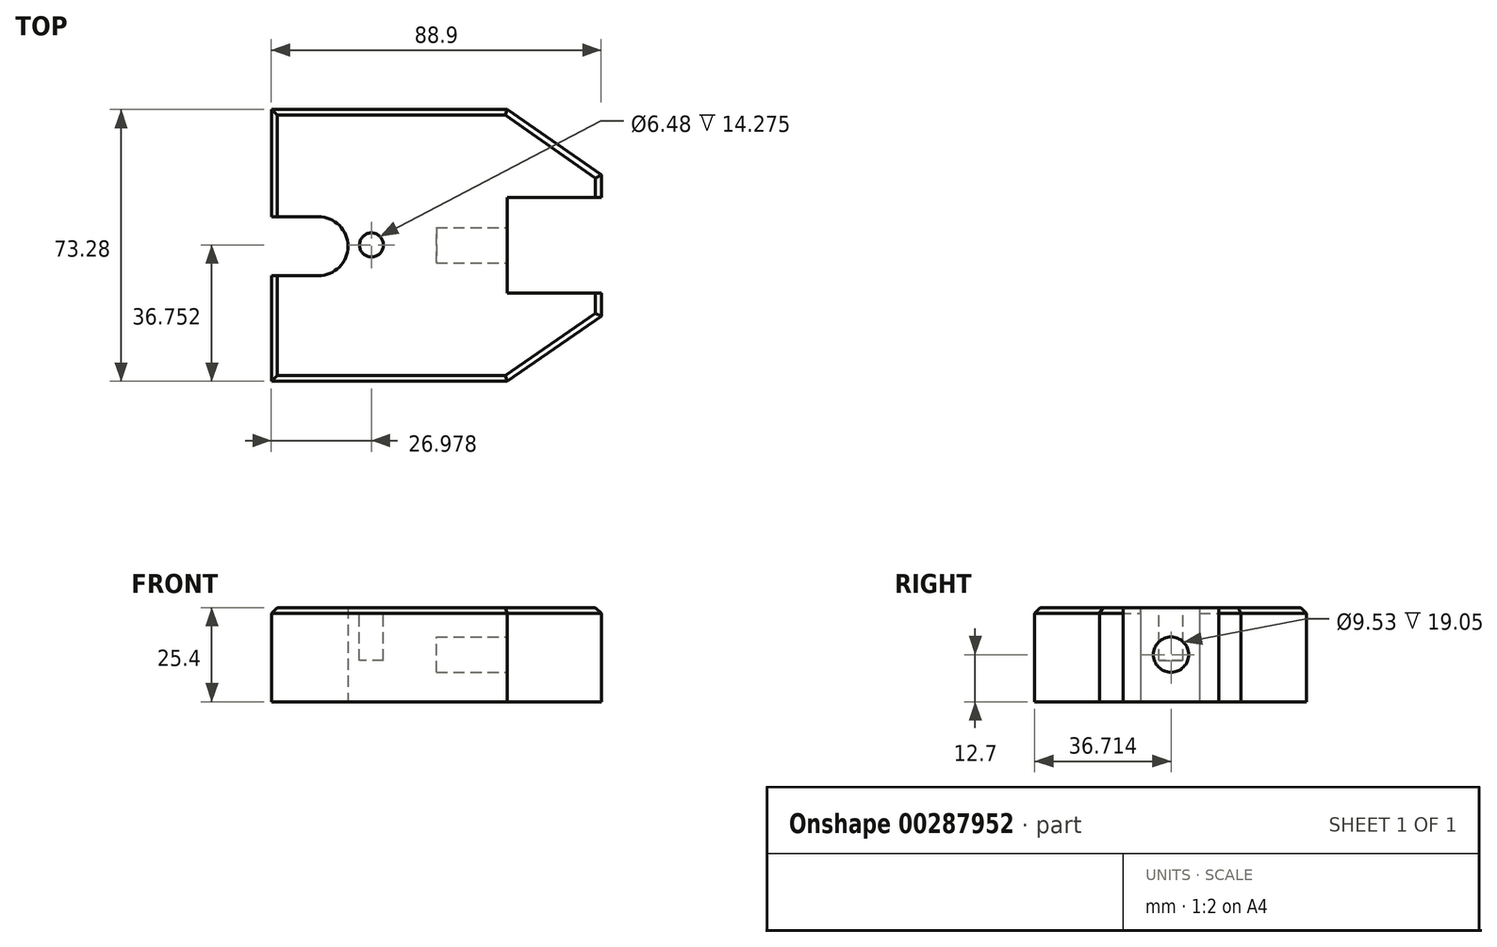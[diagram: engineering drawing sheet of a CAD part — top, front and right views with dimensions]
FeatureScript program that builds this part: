
annotation { "Feature Type Name" : "Feature", "Feature Type Description" : "" }
export const myFeature = defineFeature(function(context is Context, id is Id, definition is map)
    precondition{}
    {
        {
            var Q0;
            Q0=qCreatedBy(makeId("Top.planeOp"),FACE);
            var sketch = newSketch(context, id + "F0", { "sketchPlane" : qUnion([Q0])});
            skLineSegment(sketch, "E0.bottom", {"start": v(-102.85, 91.05) * mm, "end": v(-13.95, 91.05) * mm});
            skLineSegment(sketch, "E0.top", {"start": v(-102.85, 17.77) * mm, "end": v(-13.95, 17.77) * mm});
            skLineSegment(sketch, "E0.left", {"start": v(-102.85, 91.05) * mm, "end": v(-102.85, 17.77) * mm});
            skLineSegment(sketch, "E0.right", {"start": v(-13.95, 91.05) * mm, "end": v(-13.95, 17.77) * mm});
            skLineSegment(sketch, "E1.bottom", {"start": v(-13.95, 67.37) * mm, "end": v(-39.35, 67.37) * mm});
            skLineSegment(sketch, "E1.top", {"start": v(-13.95, 41.6) * mm, "end": v(-39.35, 41.6) * mm});
            skLineSegment(sketch, "E1.left", {"start": v(-13.95, 67.37) * mm, "end": v(-13.95, 41.6) * mm});
            skLineSegment(sketch, "E1.right", {"start": v(-39.35, 67.37) * mm, "end": v(-39.35, 41.6) * mm});
            skLineSegment(sketch, "E2", {"start": v(-13.95, 73.4) * mm, "end": v(-39.35, 91.05) * mm});
            skLineSegment(sketch, "E3", {"start": v(-13.95, 35.3) * mm, "end": v(-39.35, 17.77) * mm});
            skLineSegment(sketch, "E4", {"start": v(-133.5, 54.52) * mm, "end": v(33.35, 54.52) * mm, "construction": true});
            skLineSegment(sketch, "E5", {"start": v(-90.15, 65.78) * mm, "end": v(-90.15, 42.58) * mm, "construction": true});
            skArc(sketch, "E6", {"start": v(-90.15, 46.23) * mm, "mid": v(-82.2, 54.18) * mm, "end": v(-90.15, 62.13) * mm});
            skLineSegment(sketch, "E7", {"start": v(-90.15, 62.13) * mm, "end": v(-102.85, 62.13) * mm});
            skLineSegment(sketch, "E8", {"start": v(-102.85, 62.13) * mm, "end": v(-102.85, 46.23) * mm});
            skLineSegment(sketch, "E9", {"start": v(-102.85, 46.23) * mm, "end": v(-90.15, 46.23) * mm});
            skSolve(sketch);
        }
        {
            var Q0;
            {var subQ1=sQuery(id+"F0.wireOp",EDGE,"E1.bottom");Q0=makeQuery(id+"F0.imprint","IMPRINT",FACE,{"disambiguationData":[TD([[makeQuery(id+"F0.imprint","IMPRINT",EDGE,{"derivedFrom":subQ1}),-1.0]])]});}
            extrude(context, id + "F1", {"entities" : qUnion([Q0]), "depth" : 25.4 * mm, "offsetDistance" : 25.4 * mm});
        }
        {
            var Q0;
            Q0=makeQuery(id+"F1.opExtrude","CAP_EDGE",EDGE,{"disambiguationData":[OSD([sQuery(id+"F0.wireOp",EDGE,"E0.top")])],"isStart":false});
            var Q1;
            Q1=makeQuery(id+"F1.opExtrude","CAP_EDGE",EDGE,{"disambiguationData":[OSD([sQuery(id+"F0.wireOp",EDGE,"E3")])],"isStart":false});
            var Q2;
            {var subQ0=sQuery(id+"F0.wireOp",EDGE,"E0.right");Q2=makeQuery(id+"F1.opExtrude","CAP_EDGE",EDGE,{"disambiguationData":[OSD([subQ0]),TDD([makeQuery(id+"F0.imprint","IMPRINT",EDGE,{"disambiguationData":[TD([[makeQuery(id+"F0.imprint","INTERSECT",VERTEX,{"derivedFrom":[subQ0,sQuery(id+"F0.wireOp",EDGE,"E3")]}),1.0]])],"derivedFrom":subQ0})])],"isStart":false});}
            var Q3;
            {var subQ0=sQuery(id+"F0.wireOp",EDGE,"E0.right");Q3=makeQuery(id+"F1.opExtrude","CAP_EDGE",EDGE,{"disambiguationData":[OSD([subQ0]),TDD([makeQuery(id+"F0.imprint","IMPRINT",EDGE,{"disambiguationData":[TD([[makeQuery(id+"F0.imprint","INTERSECT",VERTEX,{"derivedFrom":[subQ0,sQuery(id+"F0.wireOp",EDGE,"E2")]}),-1.0]])],"derivedFrom":subQ0})])],"isStart":false});}
            var Q4;
            Q4=makeQuery(id+"F1.opExtrude","CAP_EDGE",EDGE,{"disambiguationData":[OSD([sQuery(id+"F0.wireOp",EDGE,"E2")])],"isStart":false});
            var Q5;
            Q5=makeQuery(id+"F1.opExtrude","CAP_EDGE",EDGE,{"disambiguationData":[OSD([sQuery(id+"F0.wireOp",EDGE,"E0.bottom")])],"isStart":false});
            var Q6;
            {var subQ0=sQuery(id+"F0.wireOp",EDGE,"E0.left");Q6=makeQuery(id+"F1.opExtrude","CAP_EDGE",EDGE,{"disambiguationData":[OSD([subQ0]),TDD([makeQuery(id+"F0.imprint","IMPRINT",EDGE,{"disambiguationData":[TD([[makeQuery(id+"F0.imprint","INTERSECT",VERTEX,{"derivedFrom":[sQuery(id+"F0.wireOp",EDGE,"E0.top"),subQ0]}),1.0]])],"derivedFrom":subQ0})])],"isStart":false});}
            var Q7;
            {var subQ0=sQuery(id+"F0.wireOp",EDGE,"E0.left");Q7=makeQuery(id+"F1.opExtrude","CAP_EDGE",EDGE,{"disambiguationData":[OSD([subQ0]),TDD([makeQuery(id+"F0.imprint","IMPRINT",EDGE,{"disambiguationData":[TD([[makeQuery(id+"F0.imprint","INTERSECT",VERTEX,{"derivedFrom":[sQuery(id+"F0.wireOp",EDGE,"E0.bottom"),subQ0]}),-1.0]])],"derivedFrom":subQ0})])],"isStart":false});}
            chamfer(context, id + "F2", {"entities" : qUnion([Q0, Q1, Q2, Q3, Q4, Q5, Q6, Q7]), "width" : 1.52 * mm, "tangentPropagation" : true});
        }
        {
            var Q0;
            Q0=makeQuery(id+"F1.opExtrude","SWEPT_FACE",FACE,{"disambiguationData":[OSD([sQuery(id+"F0.wireOp",EDGE,"E1.right")])]});
            var sketch = newSketch(context, id + "F3", { "sketchPlane" : qUnion([Q0])});
            skLineSegment(sketch, "E10", {"start": v(54.48, 39.22) * mm, "end": v(54.48, -16.42) * mm, "construction": true});
            skLineSegment(sketch, "E11", {"start": v(-3.77, 12.7) * mm, "end": v(131.49, 12.7) * mm, "construction": true});
            skCircle(sketch, "E12", {"center": v(54.48, 12.7) * mm, "radius": 4.76 * mm});
            skSolve(sketch);
        }
        {
            var Q0;
            Q0=makeQuery(id+"F3.imprint","IMPRINT",FACE,{"disambiguationData":[TD([[makeQuery(id+"F3.imprint","IMPRINT",EDGE,{"derivedFrom":sQuery(id+"F3.wireOp",EDGE,"E12")}),1.0]])]});
            extrude(context, id + "F4", {"entities" : qUnion([Q0]), "operationType" : NewBodyOperationType.REMOVE, "oppositeDirection" : true, "depth" : 19.05 * mm, "offsetDistance" : 25.4 * mm});
        }
        {
            var Q0;
            Q0=makeQuery(id+"F1.opExtrude","CAP_FACE",FACE,{"disambiguationData":[OSD([sQuery(id+"F0.wireOp",EDGE,"E0.bottom"),sQuery(id+"F0.wireOp",EDGE,"E0.top"),sQuery(id+"F0.wireOp",EDGE,"E0.left"),sQuery(id+"F0.wireOp",EDGE,"E0.right"),sQuery(id+"F0.wireOp",EDGE,"E1.bottom"),sQuery(id+"F0.wireOp",EDGE,"E1.top"),sQuery(id+"F0.wireOp",EDGE,"E1.right"),sQuery(id+"F0.wireOp",EDGE,"E2"),sQuery(id+"F0.wireOp",EDGE,"E3"),sQuery(id+"F0.wireOp",EDGE,"E6"),sQuery(id+"F0.wireOp",EDGE,"E7"),sQuery(id+"F0.wireOp",EDGE,"E9")])],"isStart":false});
            var sketch = newSketch(context, id + "F5", { "sketchPlane" : qUnion([Q0])});
            skCircle(sketch, "E13", {"center": v(-75.87, 54.52) * mm, "radius": 3.24 * mm});
            skSolve(sketch);
        }
        {
            var Q0;
            Q0=makeQuery(id+"F5.imprint","IMPRINT",FACE,{"disambiguationData":[TD([[makeQuery(id+"F5.imprint","IMPRINT",EDGE,{"derivedFrom":sQuery(id+"F5.wireOp",EDGE,"E13")}),1.0]])]});
            extrude(context, id + "F6", {"entities" : qUnion([Q0]), "operationType" : NewBodyOperationType.REMOVE, "oppositeDirection" : true, "depth" : 14.27 * mm, "offsetDistance" : 25.4 * mm});
        }
    });
